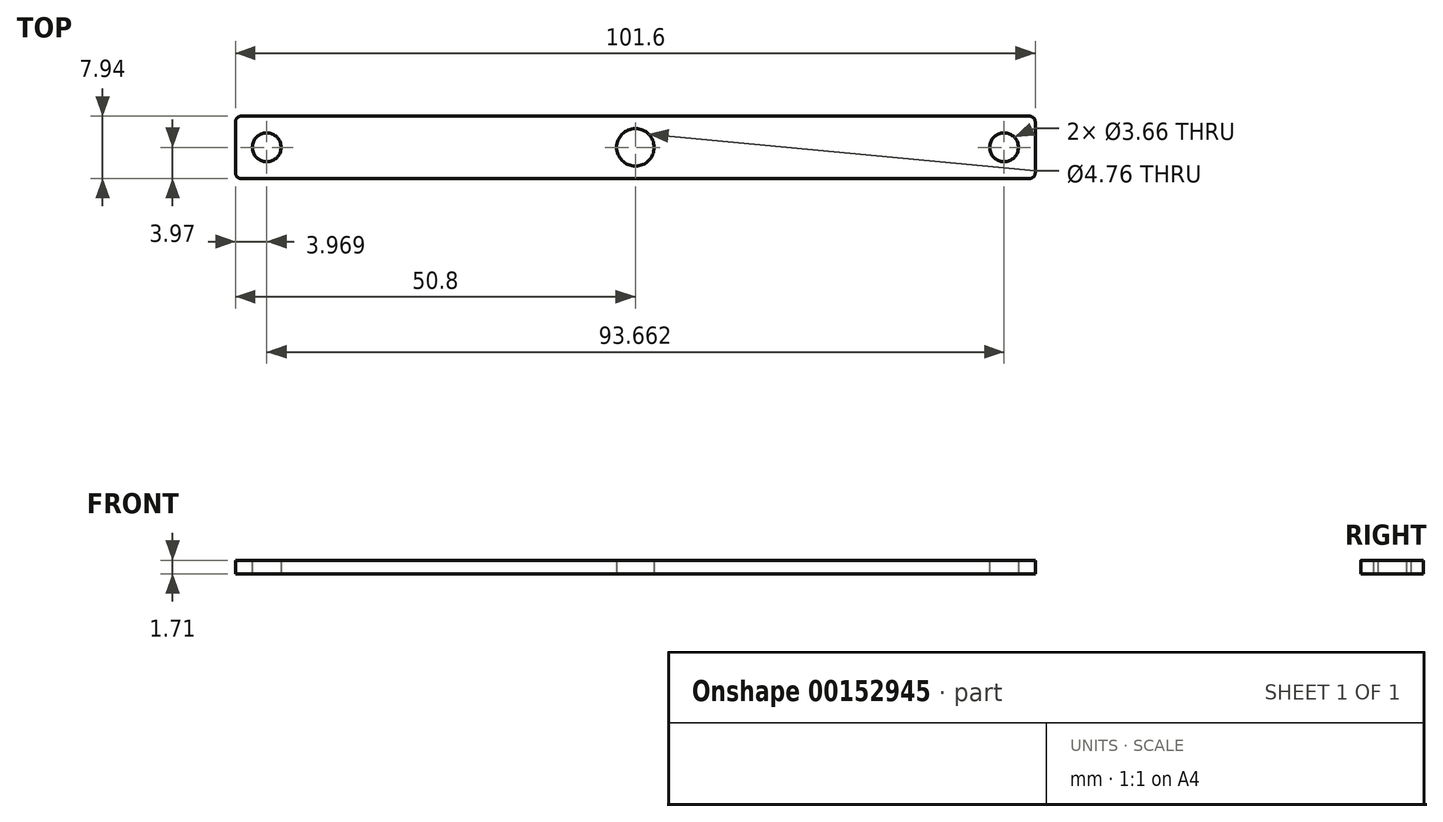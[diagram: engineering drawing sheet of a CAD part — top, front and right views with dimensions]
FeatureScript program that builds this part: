
annotation { "Feature Type Name" : "Feature", "Feature Type Description" : "" }
export const myFeature = defineFeature(function(context is Context, id is Id, definition is map)
    precondition{}
    {
        {
            var Q0;
            Q0=qCreatedBy(makeId("Top.planeOp"),FACE);
            var sketch = newSketch(context, id + "F0", { "sketchPlane" : qUnion([Q0])});
            skLineSegment(sketch, "E0.bottom", {"start": v(50.8, -3.97) * mm, "end": v(-50.8, -3.97) * mm});
            skLineSegment(sketch, "E0.top", {"start": v(50.8, 3.97) * mm, "end": v(-50.8, 3.97) * mm});
            skLineSegment(sketch, "E0.left", {"start": v(50.8, -3.97) * mm, "end": v(50.8, 3.97) * mm});
            skLineSegment(sketch, "E0.right", {"start": v(-50.8, -3.97) * mm, "end": v(-50.8, 3.97) * mm});
            skPoint(sketch, "E0.middle", {"position": v(0, 0) * mm});
            skLineSegment(sketch, "E1", {"start": v(-50.8, 0) * mm, "end": v(-46.83, 0) * mm, "construction": true});
            skLineSegment(sketch, "E2", {"start": v(-46.83, 0) * mm, "end": v(-46.83, -3.97) * mm, "construction": true});
            skLineSegment(sketch, "E3", {"start": v(50.8, 0) * mm, "end": v(46.83, 0) * mm, "construction": true});
            skCircle(sketch, "E4", {"center": v(-46.83, 0) * mm, "radius": 1.83 * mm});
            skCircle(sketch, "E5", {"center": v(46.83, 0) * mm, "radius": 1.83 * mm});
            skCircle(sketch, "E6", {"center": v(0, 0) * mm, "radius": 2.38 * mm});
            skSolve(sketch);
        }
        {
            var Q0;
            Q0 = qSketchRegion(id + "F0", true);
            extrude(context, id + "F1", {"entities" : qUnion([Q0]), "depth" : 1.7 * mm});
        }
        {
            var Q0;
            Q0=makeQuery(id+"F1.opExtrude","SWEPT_EDGE",EDGE,{"disambiguationData":[OSD([sQuery(id+"F0.wireOp",EDGE,"E0.top"),sQuery(id+"F0.wireOp",EDGE,"E0.left")])]});
            var Q1;
            Q1=makeQuery(id+"F1.opExtrude","SWEPT_EDGE",EDGE,{"disambiguationData":[OSD([sQuery(id+"F0.wireOp",EDGE,"E0.top"),sQuery(id+"F0.wireOp",EDGE,"E0.right")])]});
            var Q2;
            Q2=makeQuery(id+"F1.opExtrude","SWEPT_EDGE",EDGE,{"disambiguationData":[OSD([sQuery(id+"F0.wireOp",EDGE,"E0.bottom"),sQuery(id+"F0.wireOp",EDGE,"E0.right")])]});
            var Q3;
            Q3=makeQuery(id+"F1.opExtrude","SWEPT_EDGE",EDGE,{"disambiguationData":[OSD([sQuery(id+"F0.wireOp",EDGE,"E0.bottom"),sQuery(id+"F0.wireOp",EDGE,"E0.left")])]});
            fillet(context, id + "F2", {"entities" : qUnion([Q0, Q1, Q2, Q3]), "radius" : 0.76 * mm, "tangentPropagation" : true, "allowEdgeOverflow" : false});
        }
    });
